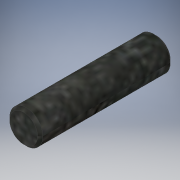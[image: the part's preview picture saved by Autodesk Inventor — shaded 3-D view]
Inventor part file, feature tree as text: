
AUTODESK INVENTOR PART (.ipt)
format: ipt  version: 2019.4 (Build 234330000, 330)  size: 111,104 bytes
history: native  units: in
note: dims shown in document units (in); Inventor stores cm internally (conversion verified against a paired STEP export)
features: extrude x1, chamfer x1, sketch x1
ambient origin geometry x8: Origin, YZ Plane, XZ Plane, XY Plane, X Axis, Y Axis, Z Axis, Center Point
bodies: Solid1 (feature_tree)
feature tree (3):
  extrude  "Extrusion1"  Depth=1.0in TaperAngle=0.0deg
  chamfer  "Chamfer1"  Distance=0.125in Angle=45.0deg
  sketch  "Sketch1"  dims[d0=0.25in d1=1.0in d2=0.0in d3=0.02in d4=0.125in d5=45.0deg]
